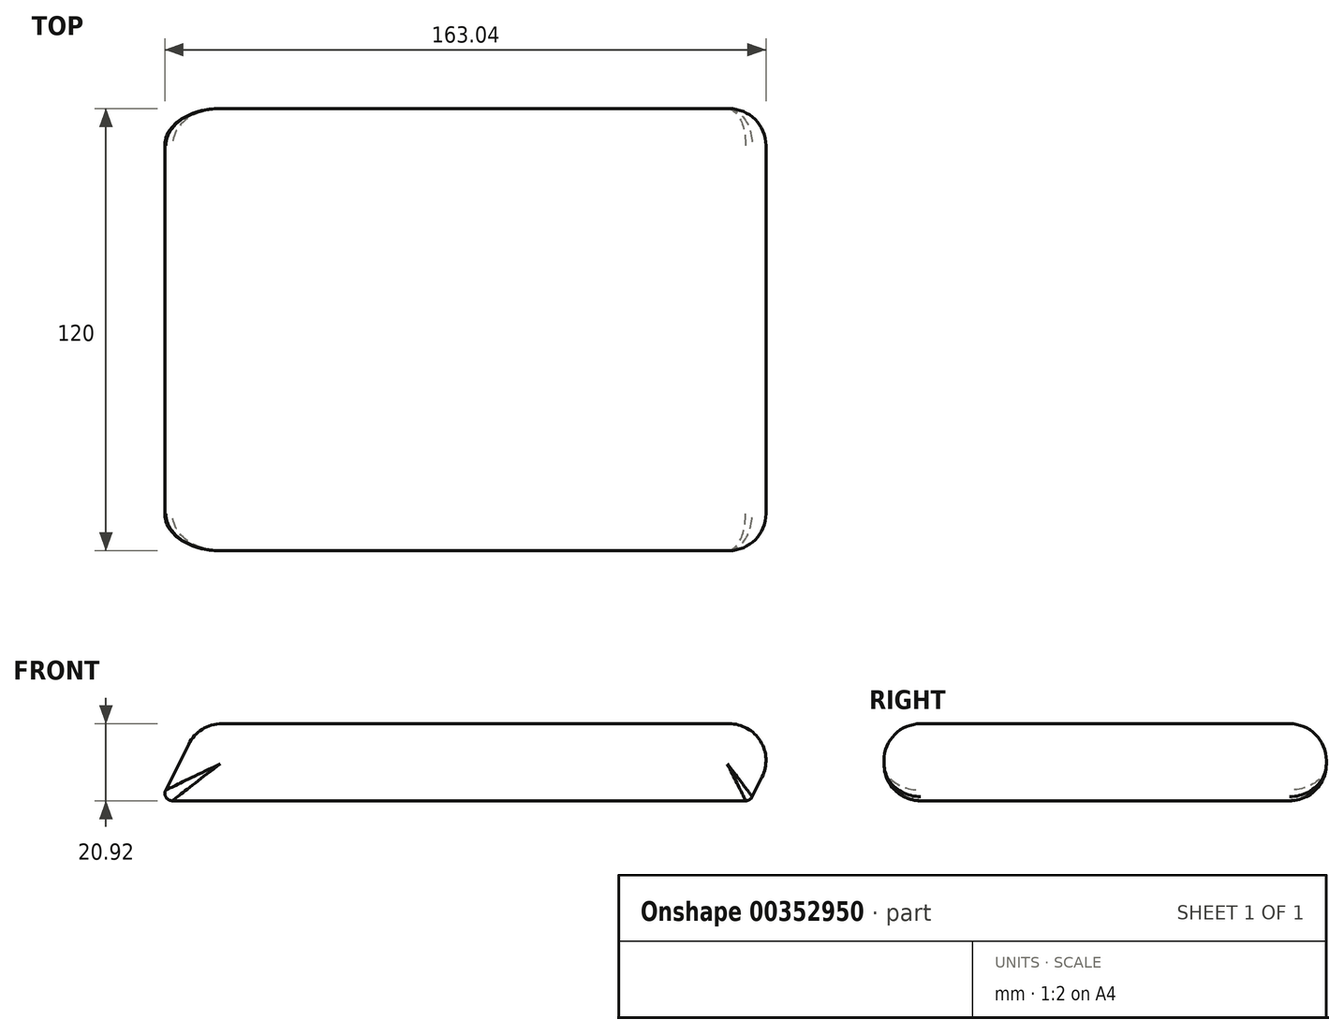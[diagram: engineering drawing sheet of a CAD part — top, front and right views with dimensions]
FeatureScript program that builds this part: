
annotation { "Feature Type Name" : "Feature", "Feature Type Description" : "" }
export const myFeature = defineFeature(function(context is Context, id is Id, definition is map)
    precondition{}
    {
        {
            var Q0;
            Q0=qCreatedBy(makeId("Front.planeOp"),FACE);
            var sketch = newSketch(context, id + "F0", { "sketchPlane" : qUnion([Q0])});
            skLineSegment(sketch, "E0", {"start": v(-77.99, 0) * mm, "end": v(82.01, 0) * mm});
            skLineSegment(sketch, "E1", {"start": v(-77.99, 0) * mm, "end": v(-67.53, 20.92) * mm});
            skLineSegment(sketch, "E2", {"start": v(-67.53, 20.92) * mm, "end": v(92.47, 20.92) * mm});
            skLineSegment(sketch, "E3", {"start": v(92.47, 20.92) * mm, "end": v(82.01, 0) * mm});
            skSolve(sketch);
        }
        {
            var Q0;
            Q0=makeQuery(id+"F0.imprint","IMPRINT",FACE,{"disambiguationData":[TD([[makeQuery(id+"F0.imprint","IMPRINT",EDGE,{"derivedFrom":sQuery(id+"F0.wireOp",EDGE,"E0")}),1.0]])]});
            extrude(context, id + "F1", {"entities" : qUnion([Q0]), "depth" : 120 * mm});
        }
        {
            var Q0;
            Q0=makeQuery(id+"F1.opExtrude","SWEPT_EDGE",EDGE,{"disambiguationData":[OSD([sQuery(id+"F0.wireOp",EDGE,"E1"),sQuery(id+"F0.wireOp",EDGE,"E2")])]});
            fillet(context, id + "F2", {"entities" : qUnion([Q0]), "radius" : 10 * mm, "tangentPropagation" : true, "allowEdgeOverflow" : false});
        }
        {
            var Q0;
            Q0=makeQuery(id+"F1.opExtrude","SWEPT_EDGE",EDGE,{"disambiguationData":[OSD([sQuery(id+"F0.wireOp",EDGE,"E0"),sQuery(id+"F0.wireOp",EDGE,"E1")])]});
            fillet(context, id + "F3", {"entities" : qUnion([Q0]), "radius" : 2 * mm, "tangentPropagation" : true, "allowEdgeOverflow" : false});
        }
        {
            var Q0;
            Q0=makeQuery(id+"F1.opExtrude","SWEPT_EDGE",EDGE,{"disambiguationData":[OSD([sQuery(id+"F0.wireOp",EDGE,"E0"),sQuery(id+"F0.wireOp",EDGE,"E3")])]});
            fillet(context, id + "F4", {"entities" : qUnion([Q0]), "radius" : 2 * mm, "tangentPropagation" : true, "allowEdgeOverflow" : false});
        }
        {
            var Q0;
            Q0=makeQuery(id+"F1.opExtrude","SWEPT_EDGE",EDGE,{"disambiguationData":[OSD([sQuery(id+"F0.wireOp",EDGE,"E2"),sQuery(id+"F0.wireOp",EDGE,"E3")])]});
            var Q1;
            Q1=makeQuery(id+"F1.opExtrude","CAP_EDGE",EDGE,{"disambiguationData":[OSD([sQuery(id+"F0.wireOp",EDGE,"E2")])],"isStart":true});
            var Q2;
            Q2=makeQuery(id+"F1.opExtrude","CAP_EDGE",EDGE,{"disambiguationData":[OSD([sQuery(id+"F0.wireOp",EDGE,"E2")])],"isStart":false});
            var Q3;
            Q3=makeQuery(id+"F1.opExtrude","CAP_EDGE",EDGE,{"disambiguationData":[OSD([sQuery(id+"F0.wireOp",EDGE,"E0")])],"isStart":true});
            var Q4;
            Q4=makeQuery(id+"F1.opExtrude","CAP_EDGE",EDGE,{"disambiguationData":[OSD([sQuery(id+"F0.wireOp",EDGE,"E0")])],"isStart":false});
            fillet(context, id + "F5", {"entities" : qUnion([Q0, Q1, Q2, Q3, Q4]), "radius" : 10 * mm, "tangentPropagation" : true, "allowEdgeOverflow" : false});
        }
    });
